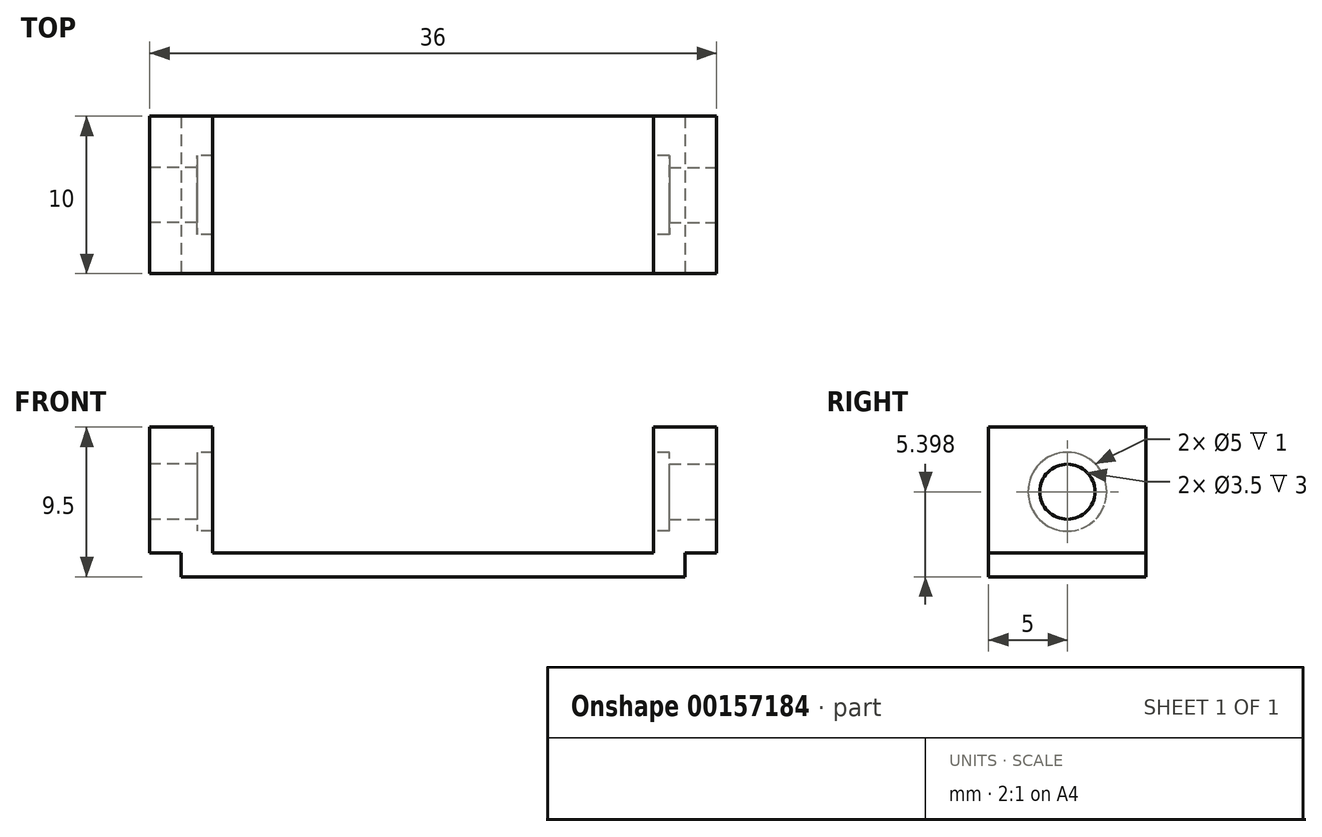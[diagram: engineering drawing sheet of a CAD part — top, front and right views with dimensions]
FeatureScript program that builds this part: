
annotation { "Feature Type Name" : "Feature", "Feature Type Description" : "" }
export const myFeature = defineFeature(function(context is Context, id is Id, definition is map)
    precondition{}
    {
        {
            var Q0;
            Q0=qCreatedBy(makeId("Top.planeOp"),FACE);
            var sketch = newSketch(context, id + "F0", { "sketchPlane" : qUnion([Q0])});
            skLineSegment(sketch, "E0.bottom", {"start": v(-16, 5) * mm, "end": v(16, 5) * mm});
            skLineSegment(sketch, "E0.top", {"start": v(-16, -5) * mm, "end": v(16, -5) * mm});
            skLineSegment(sketch, "E0.left", {"start": v(-16, 5) * mm, "end": v(-16, -5) * mm});
            skLineSegment(sketch, "E0.right", {"start": v(16, 5) * mm, "end": v(16, -5) * mm});
            skPoint(sketch, "E0.middle", {"position": v(0, 0) * mm});
            skSolve(sketch);
        }
        {
            var Q0;
            Q0 = qSketchRegion(id + "F0", true);
            extrude(context, id + "F1", {"entities" : qUnion([Q0]), "depth" : 1.5 * mm});
        }
        {
            var Q0;
            Q0=makeQuery(id+"F1.opExtrude","CAP_FACE",FACE,{"disambiguationData":[OSD([sQuery(id+"F0.wireOp",EDGE,"E0.bottom"),sQuery(id+"F0.wireOp",EDGE,"E0.top"),sQuery(id+"F0.wireOp",EDGE,"E0.left"),sQuery(id+"F0.wireOp",EDGE,"E0.right")])],"isStart":false});
            var sketch = newSketch(context, id + "F2", { "sketchPlane" : qUnion([Q0])});
            skLineSegment(sketch, "E1.bottom", {"start": v(-14, 5) * mm, "end": v(-18, 5) * mm});
            skLineSegment(sketch, "E1.top", {"start": v(-14, -5) * mm, "end": v(-18, -5) * mm});
            skLineSegment(sketch, "E1.left", {"start": v(-14, 5) * mm, "end": v(-14, -5) * mm});
            skLineSegment(sketch, "E1.right", {"start": v(-18, 5) * mm, "end": v(-18, -5) * mm});
            skLineSegment(sketch, "E2.bottom", {"start": v(14, 5) * mm, "end": v(18, 5) * mm});
            skLineSegment(sketch, "E2.top", {"start": v(14, -5) * mm, "end": v(18, -5) * mm});
            skLineSegment(sketch, "E2.left", {"start": v(14, 5) * mm, "end": v(14, -5) * mm});
            skLineSegment(sketch, "E2.right", {"start": v(18, 5) * mm, "end": v(18, -5) * mm});
            skSolve(sketch);
        }
        {
            var Q0;
            Q0 = qSketchRegion(id + "F2", true);
            extrude(context, id + "F3", {"entities" : qUnion([Q0]), "operationType" : NewBodyOperationType.ADD, "depth" : 8 * mm});
        }
        {
            var Q0;
            Q0=makeQuery(id+"F3.opExtrude","SWEPT_FACE",FACE,{"disambiguationData":[OSD([sQuery(id+"F2.wireOp",EDGE,"E1.right")])]});
            var sketch = newSketch(context, id + "F4", { "sketchPlane" : qUnion([Q0])});
            skCircle(sketch, "E3", {"center": v(0, 5.4) * mm, "radius": 2.5 * mm});
            skSolve(sketch);
        }
        {
            var Q0;
            Q0 = qSketchRegion(id + "F4", true);
            extrude(context, id + "F5", {"entities" : qUnion([Q0]), "operationType" : NewBodyOperationType.REMOVE, "oppositeDirection" : true, "depth" : 50 * mm});
        }
        {
            var Q0;
            Q0=makeQuery(id+"F3.opExtrude","SWEPT_FACE",FACE,{"disambiguationData":[OSD([sQuery(id+"F2.wireOp",EDGE,"E2.right")])]});
            var sketch = newSketch(context, id + "F6", { "sketchPlane" : qUnion([Q0])});
            skCircle(sketch, "E4", {"center": v(0, 5.4) * mm, "radius": 2.5 * mm});
            skCircle(sketch, "E5", {"center": v(0, 5.4) * mm, "radius": 1.75 * mm});
            skSolve(sketch);
        }
        {
            var Q0;
            Q0 = qSketchRegion(id + "F6", true);
            extrude(context, id + "F7", {"entities" : qUnion([Q0]), "operationType" : NewBodyOperationType.ADD, "oppositeDirection" : true, "depth" : 3 * mm});
        }
        {
            var Q0;
            Q0=makeQuery(id+"F3.opExtrude","SWEPT_FACE",FACE,{"disambiguationData":[OSD([sQuery(id+"F2.wireOp",EDGE,"E1.right")])]});
            var sketch = newSketch(context, id + "F8", { "sketchPlane" : qUnion([Q0])});
            skCircle(sketch, "E6", {"center": v(0, 5.4) * mm, "radius": 2.5 * mm});
            skCircle(sketch, "E7", {"center": v(0, 5.4) * mm, "radius": 1.75 * mm});
            skSolve(sketch);
        }
        {
            var Q0;
            Q0 = qSketchRegion(id + "F8", true);
            extrude(context, id + "F9", {"entities" : qUnion([Q0]), "operationType" : NewBodyOperationType.ADD, "oppositeDirection" : true, "depth" : 3 * mm});
        }
    });
